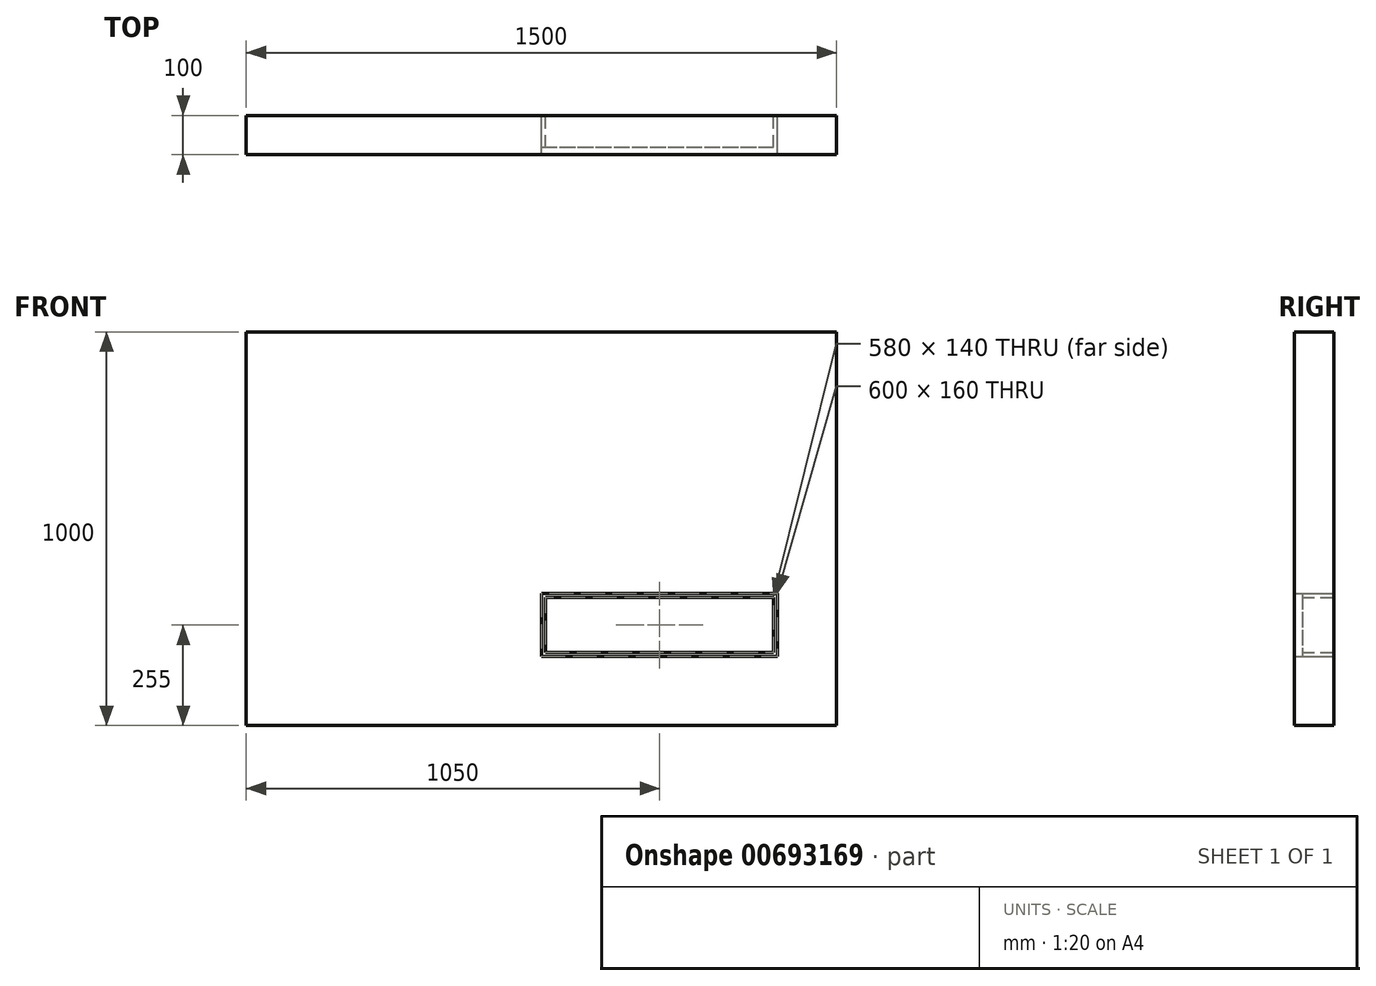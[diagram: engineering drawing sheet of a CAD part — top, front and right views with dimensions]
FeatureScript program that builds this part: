
annotation { "Feature Type Name" : "Feature", "Feature Type Description" : "" }
export const myFeature = defineFeature(function(context is Context, id is Id, definition is map)
    precondition{}
    {
        {
            var Q0;
            Q0=qCreatedBy(makeId("Front.planeOp"),FACE);
            var sketch = newSketch(context, id + "F0", { "sketchPlane" : qUnion([Q0])});
            skLineSegment(sketch, "E0.bottom", {"start": v(-750, 500) * mm, "end": v(750, 500) * mm});
            skLineSegment(sketch, "E0.top", {"start": v(-750, -500) * mm, "end": v(750, -500) * mm});
            skLineSegment(sketch, "E0.left", {"start": v(-750, 500) * mm, "end": v(-750, -500) * mm});
            skLineSegment(sketch, "E0.right", {"start": v(750, 500) * mm, "end": v(750, -500) * mm});
            skPoint(sketch, "E0.middle", {"position": v(300, -250) * mm});
            skLineSegment(sketch, "E1.bottom", {"start": v(0, -165) * mm, "end": v(600, -165) * mm});
            skLineSegment(sketch, "E1.top", {"start": v(0, -325) * mm, "end": v(600, -325) * mm});
            skLineSegment(sketch, "E1.left", {"start": v(0, -165) * mm, "end": v(0, -325) * mm});
            skLineSegment(sketch, "E1.right", {"start": v(600, -165) * mm, "end": v(600, -325) * mm});
            skPoint(sketch, "E1.middle", {"position": v(300, -245) * mm});
            skSolve(sketch);
        }
        {
            var Q0;
            Q0 = qSketchRegion(id + "F0", true);
            extrude(context, id + "F1", {"entities" : qUnion([Q0]), "depth" : 100 * mm, "offsetDistance" : 25 * mm});
        }
        {
            var Q0;
            Q0=makeQuery(id+"F1.opExtrude","CAP_FACE",FACE,{"disambiguationData":[OSD([sQuery(id+"F0.wireOp",EDGE,"E0.bottom"),sQuery(id+"F0.wireOp",EDGE,"E0.top"),sQuery(id+"F0.wireOp",EDGE,"E0.left"),sQuery(id+"F0.wireOp",EDGE,"E0.right"),sQuery(id+"F0.wireOp",EDGE,"E1.bottom"),sQuery(id+"F0.wireOp",EDGE,"E1.top"),sQuery(id+"F0.wireOp",EDGE,"E1.left"),sQuery(id+"F0.wireOp",EDGE,"E1.right")])],"isStart":true});
            var sketch = newSketch(context, id + "F2", { "sketchPlane" : qUnion([Q0])});
            skLineSegment(sketch, "E2.0", {"start": v(-10, -175) * mm, "end": v(-10, -315) * mm});
            skLineSegment(sketch, "E2.1", {"start": v(-10, -175) * mm, "end": v(-590, -175) * mm});
            skLineSegment(sketch, "E2.2", {"start": v(-590, -175) * mm, "end": v(-590, -315) * mm});
            skLineSegment(sketch, "E2.3", {"start": v(-10, -315) * mm, "end": v(-590, -315) * mm});
            skLineSegment(sketch, "E3.0", {"start": v(0, -165) * mm, "end": v(-600, -165) * mm});
            skLineSegment(sketch, "E3.1", {"start": v(0, -165) * mm, "end": v(0, -325) * mm});
            skLineSegment(sketch, "E3.2", {"start": v(0, -325) * mm, "end": v(-600, -325) * mm});
            skLineSegment(sketch, "E3.3", {"start": v(-600, -165) * mm, "end": v(-600, -325) * mm});
            skSolve(sketch);
        }
        {
            var Q0;
            Q0 = qSketchRegion(id + "F2", true);
            extrude(context, id + "F3", {"entities" : qUnion([Q0]), "oppositeDirection" : true, "depth" : 80 * mm, "offsetDistance" : 25 * mm});
        }
    });
